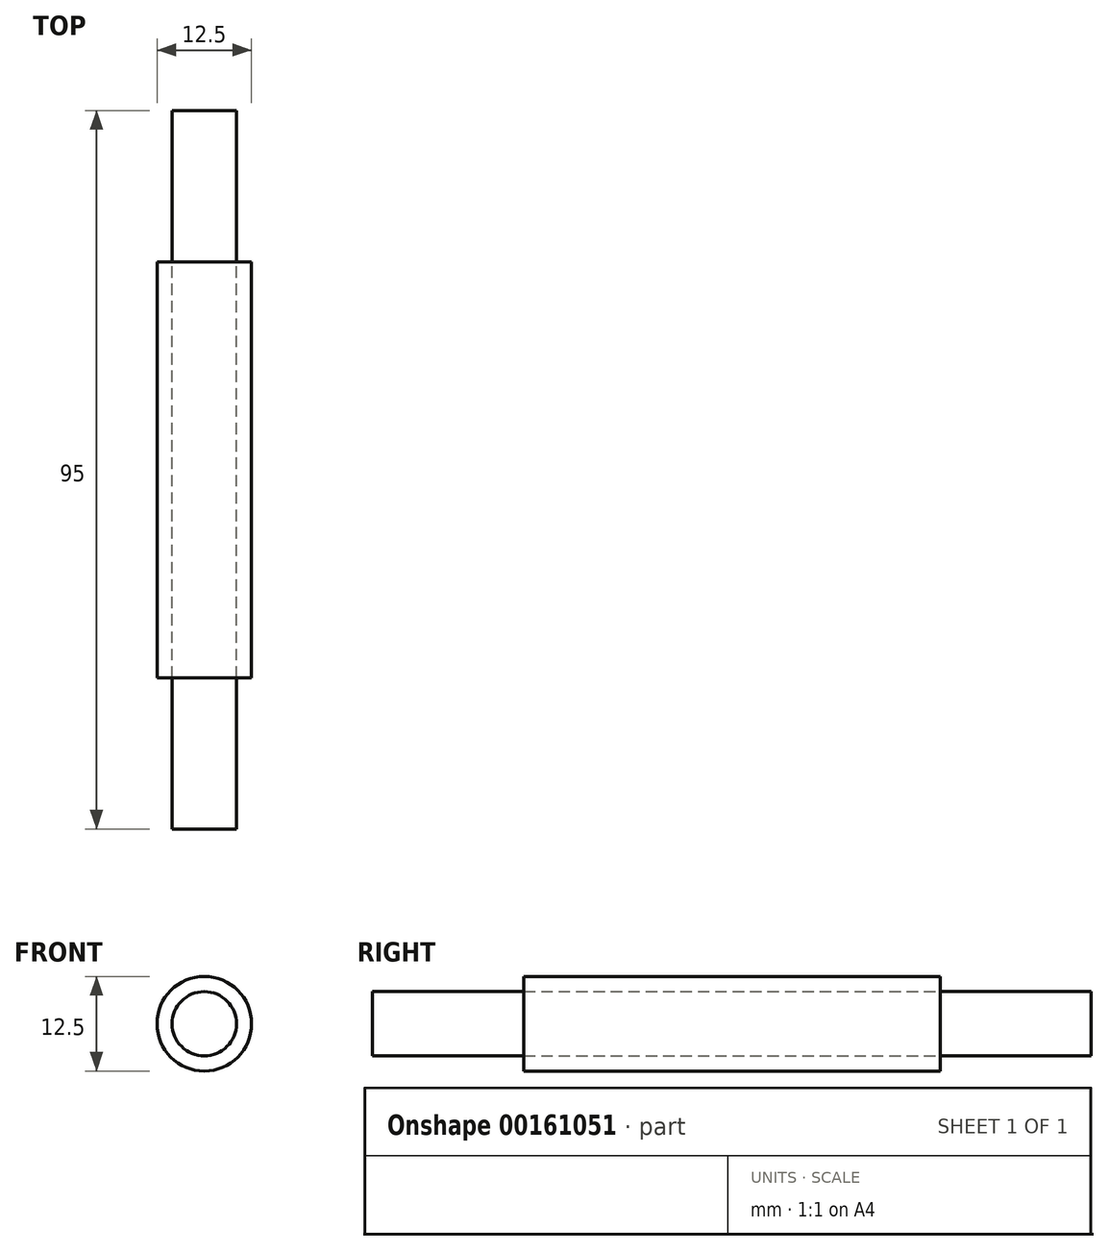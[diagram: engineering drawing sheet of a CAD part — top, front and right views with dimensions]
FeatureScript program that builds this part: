
annotation { "Feature Type Name" : "Feature", "Feature Type Description" : "" }
export const myFeature = defineFeature(function(context is Context, id is Id, definition is map)
    precondition{}
    {
        {
            var Q0;
            Q0=qCreatedBy(makeId("Front.planeOp"),FACE);
            var sketch = newSketch(context, id + "F0", { "sketchPlane" : qUnion([Q0])});
            skCircle(sketch, "E0", {"center": v(0, 0) * mm, "radius": 6.25 * mm});
            skCircle(sketch, "E1", {"center": v(0, 0) * mm, "radius": 4.25 * mm});
            skSolve(sketch);
        }
        {
            var Q0;
            Q0=makeQuery(id+"F0.imprint","IMPRINT",FACE,{"disambiguationData":[TD([[makeQuery(id+"F0.imprint","IMPRINT",EDGE,{"derivedFrom":sQuery(id+"F0.wireOp",EDGE,"E0")}),1.0]])]});
            var Q1;
            Q1=makeQuery(id+"F0.imprint","IMPRINT",FACE,{"disambiguationData":[TD([[makeQuery(id+"F0.imprint","IMPRINT",EDGE,{"derivedFrom":sQuery(id+"F0.wireOp",EDGE,"E1")}),1.0]])]});
            extrude(context, id + "F1", {"entities" : qUnion([Q0, Q1]), "endBound" : BoundingType.SYMMETRIC, "depth" : 55 * mm});
        }
        {
            var Q0;
            Q0=makeQuery(id+"F0.imprint","IMPRINT",FACE,{"disambiguationData":[TD([[makeQuery(id+"F0.imprint","IMPRINT",EDGE,{"derivedFrom":sQuery(id+"F0.wireOp",EDGE,"E1")}),1.0]])]});
            extrude(context, id + "F2", {"entities" : qUnion([Q0]), "endBound" : BoundingType.SYMMETRIC, "depth" : 95 * mm});
        }
    });
